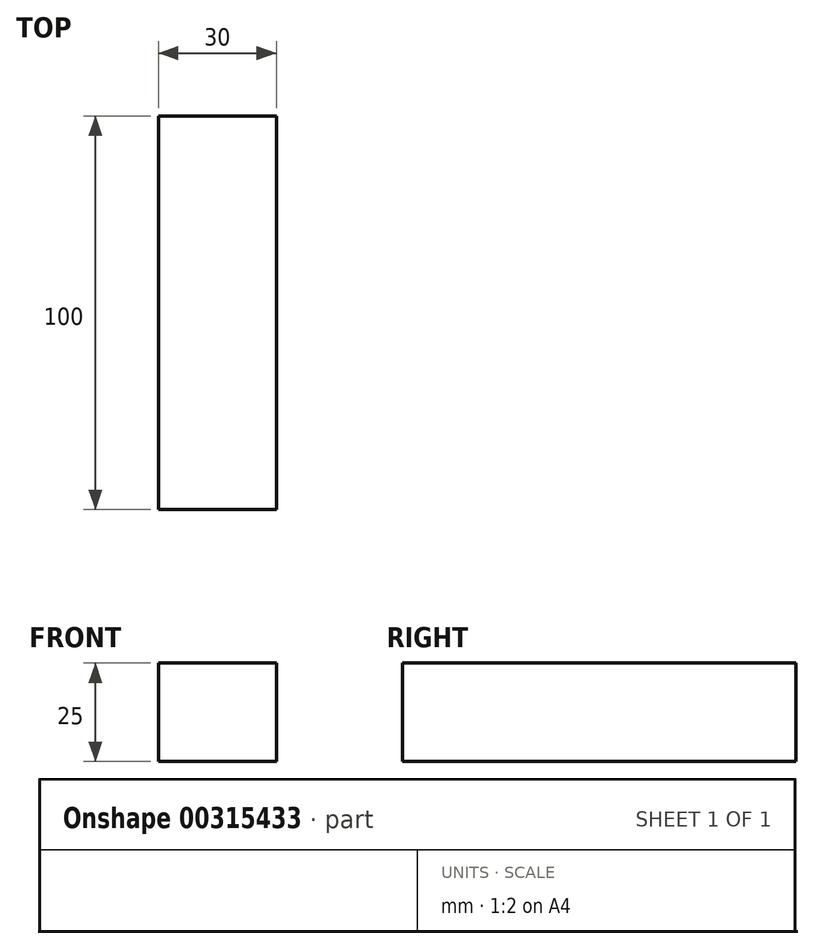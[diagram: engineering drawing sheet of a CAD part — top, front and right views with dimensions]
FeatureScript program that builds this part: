
annotation { "Feature Type Name" : "Feature", "Feature Type Description" : "" }
export const myFeature = defineFeature(function(context is Context, id is Id, definition is map)
    precondition{}
    {
        {
            var Q0;
            Q0=qCreatedBy(makeId("Top.planeOp"),FACE);
            var sketch = newSketch(context, id + "F0", { "sketchPlane" : qUnion([Q0])});
            skLineSegment(sketch, "E0.bottom", {"start": v(-15, -50) * mm, "end": v(15, -50) * mm});
            skLineSegment(sketch, "E0.top", {"start": v(-15, 50) * mm, "end": v(15, 50) * mm});
            skLineSegment(sketch, "E0.left", {"start": v(-15, -50) * mm, "end": v(-15, 50) * mm});
            skLineSegment(sketch, "E0.right", {"start": v(15, -50) * mm, "end": v(15, 50) * mm});
            skPoint(sketch, "E0.middle", {"position": v(0, 0) * mm});
            skSolve(sketch);
        }
        {
            var Q0;
            Q0 = qSketchRegion(id + "F0", true);
            extrude(context, id + "F1", {"entities" : qUnion([Q0]), "depth" : 25 * mm});
        }
    });
